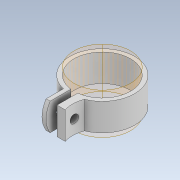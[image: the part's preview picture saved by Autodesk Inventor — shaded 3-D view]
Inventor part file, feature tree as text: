
AUTODESK INVENTOR PART (.ipt)
format: ipt  version: 2021 (Build 250183000, 183)  size: 174,080 bytes
history: native  units: mm
features: sketch x7, other x4, extrude x4, plane x1, mirror x1, split x1, revolve x1, hole x1
ambient origin geometry x8: Origin, YZ Plane, XZ Plane, XY Plane, X Axis, Y Axis, Z Axis, Center Point
bodies: Body1 (feature_tree), Body2 (feature_tree)
feature tree (20):
  other  "Sólido1"
  plane  "Plano de trabajo1"
  sketch  "Boceto3"  dims[d3=2.5mm d4=20.0mm]
  extrude  "Extrusión1"  Depth=30.0mm TaperAngle=0.0deg
  mirror  "Simetría1"
  split  "Dividir2"
  other  "Eje de trabajo1"
  revolve  "Revolución1"  [1 undecoded]
  extrude  "Extrusión2"  Depth=3.0mm TaperAngle=0.0deg
  extrude  "Extrusión3"  Depth=15.0mm
  extrude  "Extrusión4"  TaperAngle=90.0deg  [1 undecoded]
  hole  "Agujero3"  [1 undecoded]
  sketch  "Boceto1"  dims[d0=41.275mm d1=30.0mm d2=0.0mm]
  other  "Sup1"
  sketch  "Boceto5"  dims[d8=5.0mm d10=3.0mm d11=0.0mm]
  sketch  "Boceto6"  dims[d19=23.0mm d20=15.0mm]
  sketch  "Boceto8"  dims[d29=3.0mm d30=90.0deg]
  sketch  "Boceto9"  dims[d31=0.0mm d32=0.0mm d33=6.0mm]
  sketch  "Boceto10"  dims[d34=25.0mm d35=10.0mm d36=0.0mm d37=5.0mm d38=0.0mm d39=0.0mm d40=6.0mm d41=6.0mm d42=4.0mm d43=2.0mm d44=90.0deg d45=8.0mm d46=20.594885mm d47=7.5mm]
  other  "SuperficieExtrusión1"
note: 3 required parameter values undecoded (feature->parameter linkage not recoverable at this tier; creation-order binding heuristic only, values carry confidence <= 0.55)